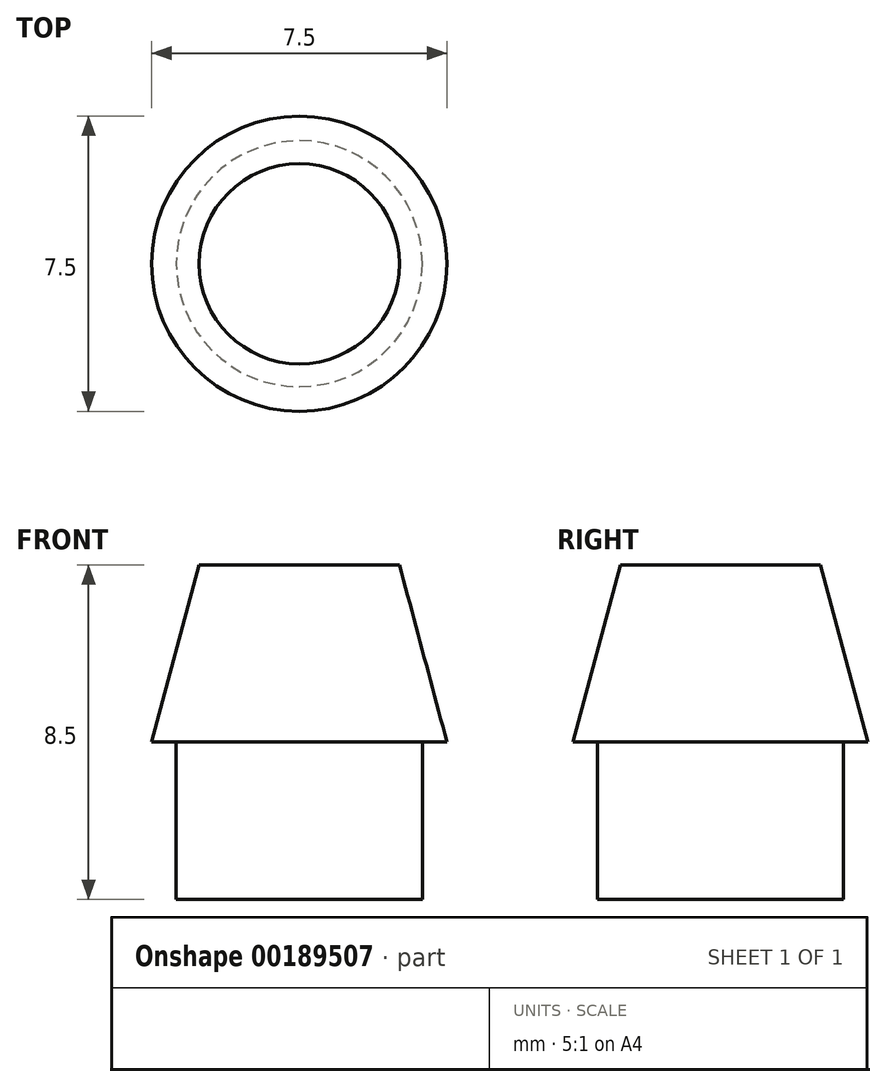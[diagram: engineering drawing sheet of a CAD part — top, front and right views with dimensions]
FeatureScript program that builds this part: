
annotation { "Feature Type Name" : "Feature", "Feature Type Description" : "" }
export const myFeature = defineFeature(function(context is Context, id is Id, definition is map)
    precondition{}
    {
        {
            assignVariable(context, id + "F0", {"name" : "peg_board_t", "anyValue" : 4});
        }
        {
            assignVariable(context, id + "F1", {"name" : "peg_pin_h", "anyValue" : 4.5});
        }
        {
            var Q0;
            Q0=qCreatedBy(makeId("Top.planeOp"),FACE);
            var sketch = newSketch(context, id + "F2", { "sketchPlane" : qUnion([Q0])});
            skCircle(sketch, "E0", {"center": v(0, 0) * mm, "radius": 3.12 * mm});
            skSolve(sketch);
        }
        {
            var Q0;
            Q0 = qSketchRegion(id + "F2", true);
            extrude(context, id + "F3", {"entities" : qUnion([Q0]), "depth" : (getVariable(context, 'peg_board_t')) * mm});
        }
        {
            var Q0;
            Q0=makeQuery(id+"F3.opExtrude","CAP_FACE",FACE,{"disambiguationData":[OSD([sQuery(id+"F2.wireOp",EDGE,"E0")])],"isStart":false});
            var sketch = newSketch(context, id + "F4", { "sketchPlane" : qUnion([Q0])});
            skCircle(sketch, "E1", {"center": v(0, 0) * mm, "radius": 3.75 * mm});
            skSolve(sketch);
        }
        {
            var Q0;
            Q0 = qSketchRegion(id + "F4", true);
            extrude(context, id + "F5", {"entities" : qUnion([Q0]), "operationType" : NewBodyOperationType.ADD, "depth" : (getVariable(context, 'peg_pin_h')) * mm, "hasDraft" : true, "draftAngle" : 15 * degree, "draftPullDirection" : true});
        }
    });
